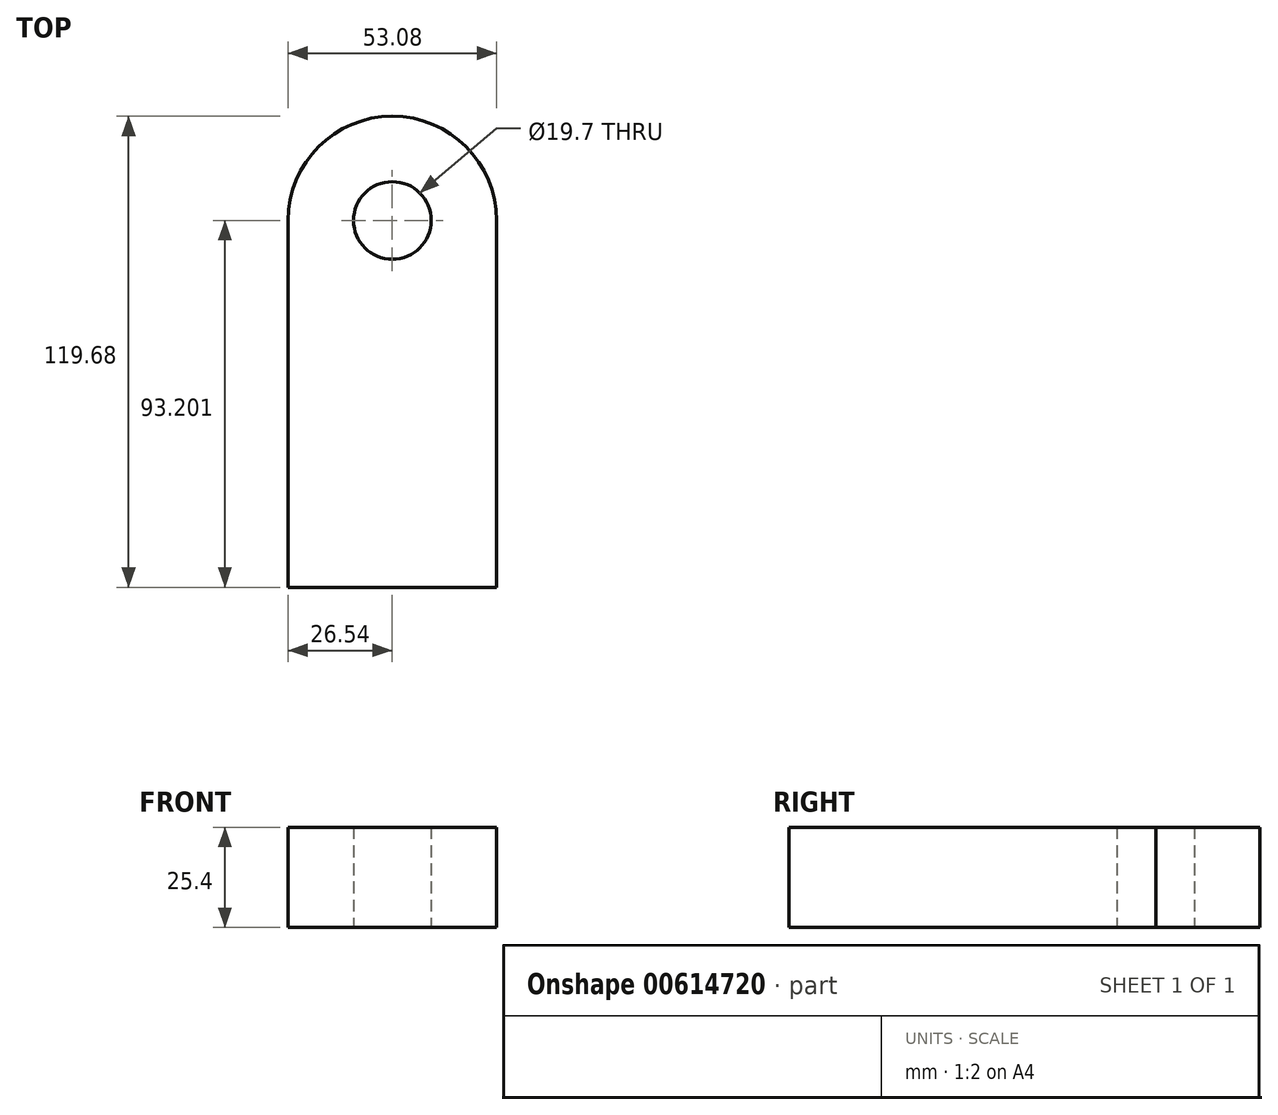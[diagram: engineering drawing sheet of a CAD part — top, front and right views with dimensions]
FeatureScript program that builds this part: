
annotation { "Feature Type Name" : "Feature", "Feature Type Description" : "" }
export const myFeature = defineFeature(function(context is Context, id is Id, definition is map)
    precondition{}
    {
        {
            var Q0;
            Q0=qCreatedBy(makeId("Top.planeOp"),FACE);
            var sketch = newSketch(context, id + "F0", { "sketchPlane" : qUnion([Q0])});
            skLineSegment(sketch, "E0.bottom", {"start": v(-26.54, 46.6) * mm, "end": v(-26.48, 46.6) * mm});
            skLineSegment(sketch, "E0.top", {"start": v(-26.54, -46.6) * mm, "end": v(26.54, -46.6) * mm});
            skLineSegment(sketch, "E0.left", {"start": v(-26.54, 46.6) * mm, "end": v(-26.54, -46.6) * mm});
            skLineSegment(sketch, "E0.right", {"start": v(26.54, 46.6) * mm, "end": v(26.54, -46.6) * mm});
            skPoint(sketch, "E0.middle", {"position": v(0, 0) * mm});
            skArc(sketch, "E1", {"start": v(26.48, 46.6) * mm, "mid": v(0, 73.08) * mm, "end": v(-26.48, 46.6) * mm});
            skLineSegment(sketch, "E2.trimOffspring", {"start": v(26.48, 46.6) * mm, "end": v(26.54, 46.6) * mm});
            skCircle(sketch, "E3", {"center": v(0, 46.6) * mm, "radius": 9.85 * mm});
            skSolve(sketch);
        }
        {
            var Q0;
            Q0 = qSketchRegion(id + "F0", true);
            extrude(context, id + "F1", {"entities" : qUnion([Q0]), "depth" : 25.4 * mm, "offsetDistance" : 25.4 * mm});
        }
    });
